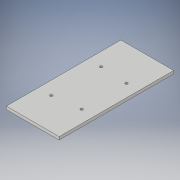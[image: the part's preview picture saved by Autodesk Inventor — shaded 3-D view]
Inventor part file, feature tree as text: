
AUTODESK INVENTOR PART (.ipt)
format: ipt  version: 2019 (Build 230136000, 136)  size: 146,944 bytes
history: native  units: mm
features: extrude x1, sketch x1
ambient origin geometry x8: Origin, YZ Plane, XZ Plane, XY Plane, X Axis, Y Axis, Z Axis, Center Point
bodies: Solid1 (feature_tree)
feature tree (2):
  extrude  "Extrusion1"  Depth=3.0mm TaperAngle=0.0deg
  sketch  "Sketch1"  dims[d1=115.0mm d2=3.0mm d3=0.0mm]
